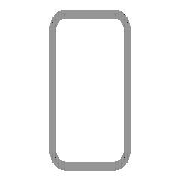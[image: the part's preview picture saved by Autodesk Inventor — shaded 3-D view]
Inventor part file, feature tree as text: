
AUTODESK INVENTOR PART (.ipt)
format: ipt  version: 2025 (Build 290162010, 162A)  size: 146,432 bytes
history: native  units: mm (DEFAULTED — no unit token found)
features: other x3, sketch x2, extrude x1, plane x1
ambient origin geometry x8: Origin, YZ Plane, XZ Plane, XY Plane, X Axis, Y Axis, Z Axis, Center Point
bodies: Solid1 (feature_tree), Body (feature_tree)
feature tree (7):
  other  "Driven Length"
  other  "Start plane"
  other  "End plane"
  extrude  "Extrusion2"  TaperAngle=0.0deg  [1 undecoded]
  sketch  "Sketch3"  dims[d3=796.0mm d4=0.0mm]
  plane  "Work Plane3"
  sketch  "Sketch5"  dims[d7=4.0mm d9=20.0mm d11=40.0mm d12=2.0mm d13=-0.0mm d14=796.0mm d15=10.0mm d16=20.0mm d17=90.0deg d18=796.0mm d19=5.846853mm d20=0.0mm d21=0.0mm]
note: 1 required parameter value undecoded (feature->parameter linkage not recoverable at this tier; creation-order binding heuristic only, values carry confidence <= 0.55)
